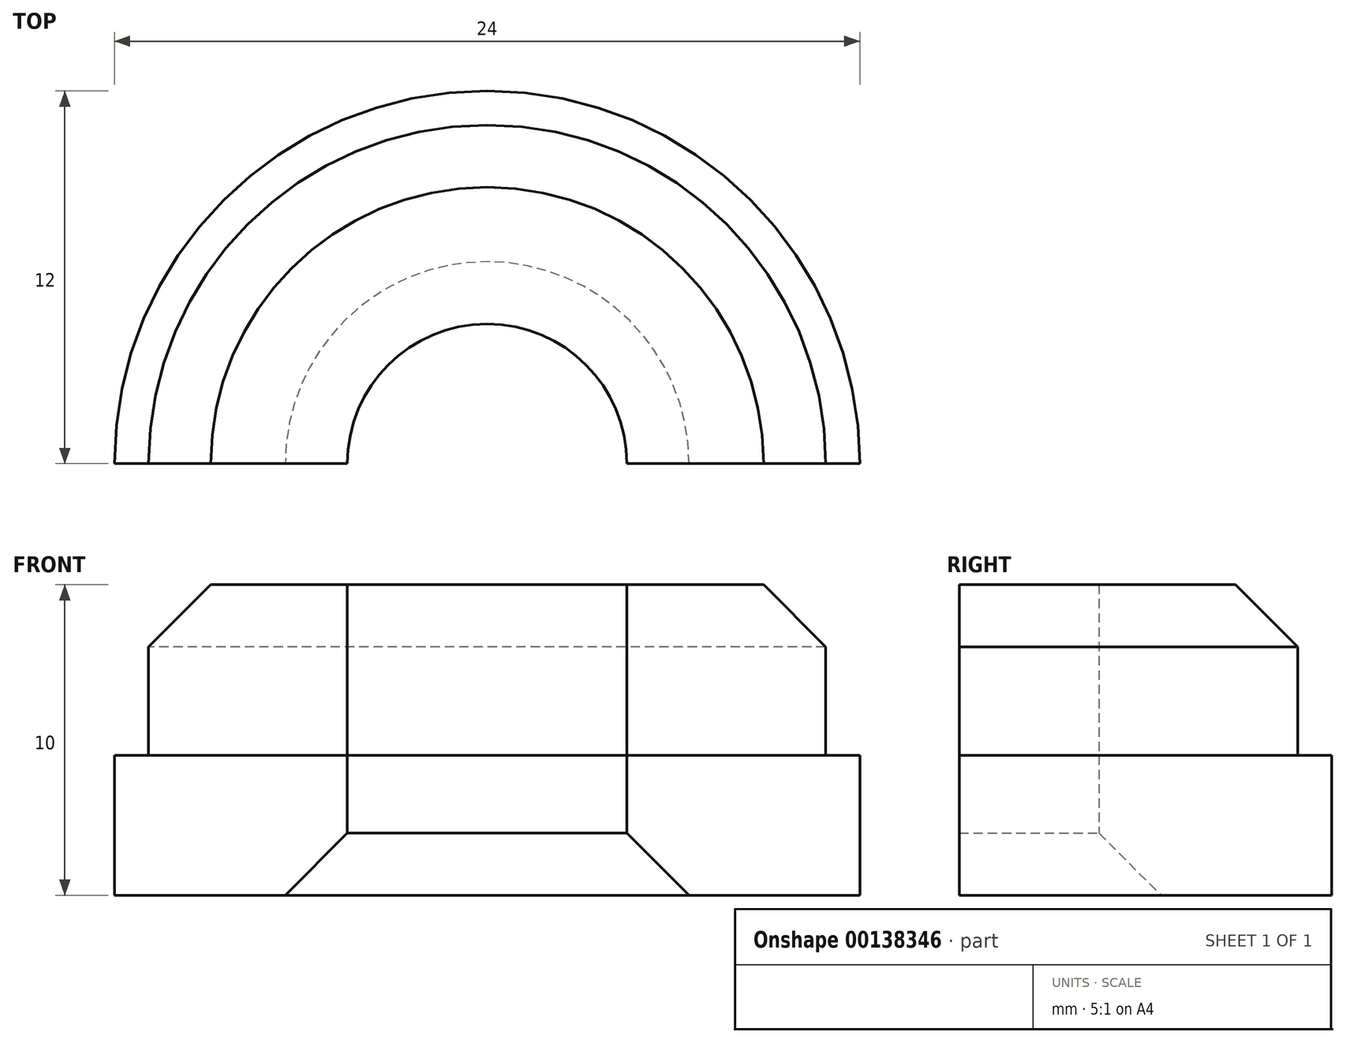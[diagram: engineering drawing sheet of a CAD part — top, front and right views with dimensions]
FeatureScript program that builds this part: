
annotation { "Feature Type Name" : "Feature", "Feature Type Description" : "" }
export const myFeature = defineFeature(function(context is Context, id is Id, definition is map)
    precondition{}
    {
        {
            var Q0;
            Q0=qCreatedBy(makeId("Top.planeOp"),FACE);
            var sketch = newSketch(context, id + "F0", { "sketchPlane" : qUnion([Q0])});
            skCircle(sketch, "E0", {"center": v(0, 0) * mm, "radius": 12 * mm});
            skCircle(sketch, "E1", {"center": v(0, 0) * mm, "radius": 4.5 * mm});
            skCircle(sketch, "E2", {"center": v(0, 0) * mm, "radius": 10.9 * mm});
            skSolve(sketch);
        }
        {
            var Q0;
            Q0 = qSketchRegion(id + "F0", true);
            var Q1;
            Q1=makeQuery(id+"F0.imprint","IMPRINT",FACE,{"disambiguationData":[TD([[makeQuery(id+"F0.imprint","IMPRINT",EDGE,{"derivedFrom":sQuery(id+"F0.wireOp",EDGE,"E1")}),-1.0]])]});
            extrude(context, id + "F1", {"entities" : qUnion([Q0, Q1]), "depth" : 4.5 * mm});
        }
        {
            var Q0;
            Q0=makeQuery(id+"F0.imprint","IMPRINT",FACE,{"disambiguationData":[TD([[makeQuery(id+"F0.imprint","IMPRINT",EDGE,{"derivedFrom":sQuery(id+"F0.wireOp",EDGE,"E1")}),-1.0]])]});
            extrude(context, id + "F2", {"entities" : qUnion([Q0]), "depth" : 10 * mm, "hasSecondDirection" : true, "secondDirectionOppositeDirection" : false, "secondDirectionDepth" : 4.5 * mm});
        }
        {
            var Q0;
            Q0=makeQuery(id+"F1.opExtrude","CAP_EDGE",EDGE,{"disambiguationData":[OSD([sQuery(id+"F0.wireOp",EDGE,"E1")])],"isStart":true});
            var Q1;
            Q1=makeQuery(id+"F2.opExtrude","CAP_EDGE",EDGE,{"disambiguationData":[OSD([sQuery(id+"F0.wireOp",EDGE,"E2")])],"isStart":false});
            chamfer(context, id + "F3", {"entities" : qUnion([Q0, Q1]), "width" : 2 * mm, "tangentPropagation" : true});
        }
        {
            var Q0;
            Q0=qCreatedBy(makeId("Top.planeOp"),FACE);
            var sketch = newSketch(context, id + "F4", { "sketchPlane" : qUnion([Q0])});
            skLineSegment(sketch, "E3.bottom", {"start": v(-21.86, 0) * mm, "end": v(20.03, 0) * mm});
            skLineSegment(sketch, "E3.top", {"start": v(-21.86, -15.03) * mm, "end": v(20.03, -15.03) * mm});
            skLineSegment(sketch, "E3.left", {"start": v(-21.86, 0) * mm, "end": v(-21.86, -15.03) * mm});
            skLineSegment(sketch, "E3.right", {"start": v(20.03, 0) * mm, "end": v(20.03, -15.03) * mm});
            skSolve(sketch);
        }
        {
            var Q0;
            Q0=makeQuery(id+"F4.imprint","IMPRINT",FACE,{"disambiguationData":[TD([[makeQuery(id+"F4.imprint","IMPRINT",EDGE,{"derivedFrom":sQuery(id+"F4.wireOp",EDGE,"E3.bottom")}),-1.0]])]});
            extrude(context, id + "F5", {"entities" : qUnion([Q0]), "operationType" : NewBodyOperationType.REMOVE, "depth" : 25 * mm});
        }
    });
